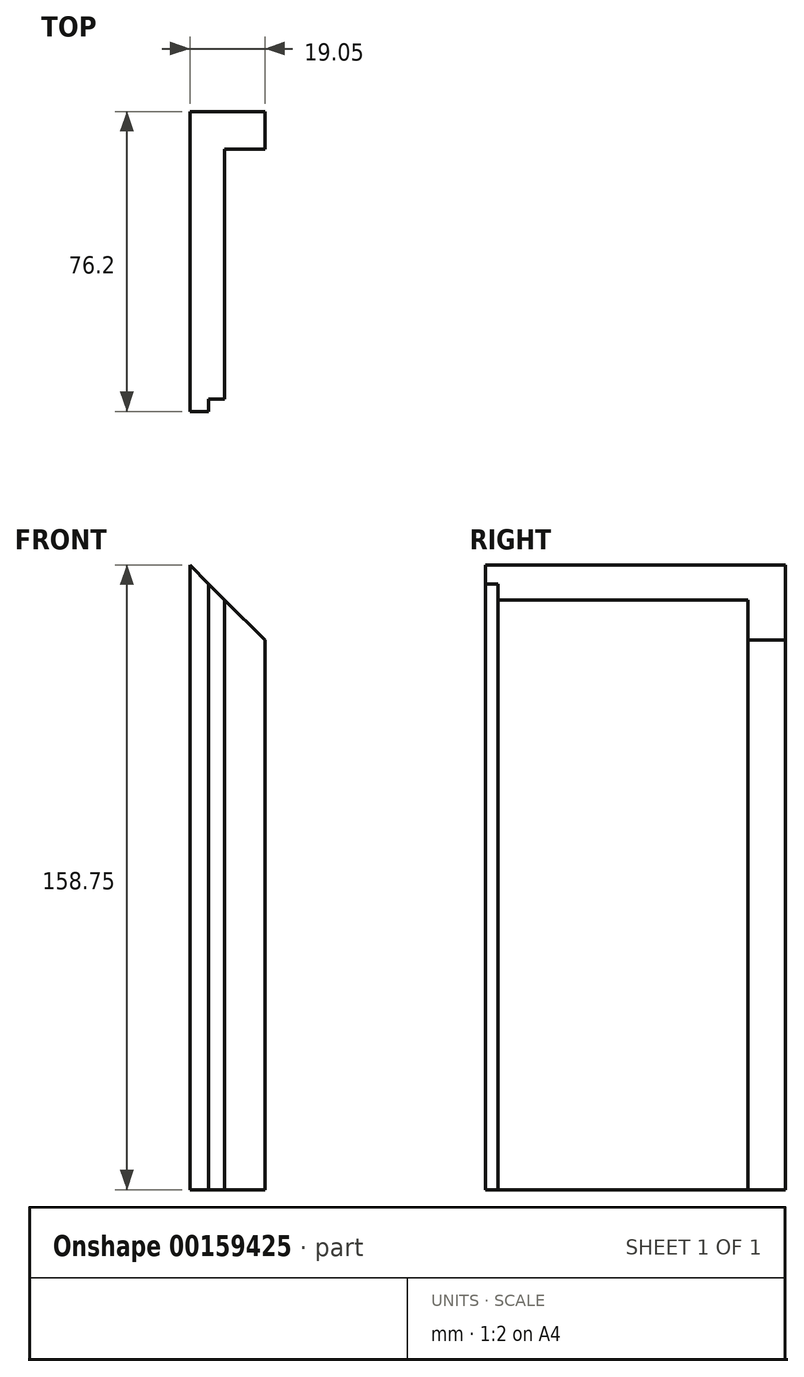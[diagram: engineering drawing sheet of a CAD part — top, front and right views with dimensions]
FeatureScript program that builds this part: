
annotation { "Feature Type Name" : "Feature", "Feature Type Description" : "" }
export const myFeature = defineFeature(function(context is Context, id is Id, definition is map)
    precondition{}
    {
        {
            var Q0;
            Q0=qCreatedBy(makeId("Front.planeOp"),FACE);
            var sketch = newSketch(context, id + "F0", { "sketchPlane" : qUnion([Q0])});
            skLineSegment(sketch, "E0", {"start": v(0, 180.55) * mm, "end": v(0, -185.02) * mm, "construction": true});
            skLineSegment(sketch, "E1", {"start": v(-187.82, 0) * mm, "end": v(184.46, 0) * mm, "construction": true});
            skLineSegment(sketch, "E2", {"start": v(0, 158.75) * mm, "end": v(-158.75, 158.75) * mm});
            skLineSegment(sketch, "E3", {"start": v(-158.75, 158.75) * mm, "end": v(-158.75, 0) * mm});
            skLineSegment(sketch, "E4", {"start": v(0, 139.7) * mm, "end": v(-139.7, 139.7) * mm});
            skLineSegment(sketch, "E5", {"start": v(-139.7, 139.7) * mm, "end": v(-139.7, 0) * mm});
            skLineSegment(sketch, "E6", {"start": v(-158.75, 0) * mm, "end": v(-139.7, 0) * mm});
            skLineSegment(sketch, "E7", {"start": v(0, 158.75) * mm, "end": v(0, 139.7) * mm});
            skSolve(sketch);
        }
        {
            var Q0;
            Q0=qSketchRegion(id+"F0",true);
            var Q1;
            Q1=qSketchRegion(id+"F2",true);
            extrude(context, id + "F1", {"entities" : qUnion([Q0, Q1]), "depth" : 76.2 * mm});
        }
        {
            var Q0;
            Q0=makeQuery(id+"F1.opExtrude","CAP_FACE",FACE,{"disambiguationData":[OSD([sQuery(id+"F0.wireOp",EDGE,"E2"),sQuery(id+"F0.wireOp",EDGE,"E3"),sQuery(id+"F0.wireOp",EDGE,"E4"),sQuery(id+"F0.wireOp",EDGE,"E5"),sQuery(id+"F0.wireOp",EDGE,"E6"),sQuery(id+"F0.wireOp",EDGE,"E7")])],"isStart":false});
            var sketch = newSketch(context, id + "F2", { "sketchPlane" : qUnion([Q0])});
            skLineSegment(sketch, "E8", {"start": v(0, -83.24) * mm, "end": v(0, 158.75) * mm, "construction": true});
            skLineSegment(sketch, "E9", {"start": v(-158.75, 0) * mm, "end": v(101.88, 0) * mm, "construction": true});
            skLineSegment(sketch, "E10.bottom", {"start": v(0, 0) * mm, "end": v(-153.92, 0) * mm});
            skLineSegment(sketch, "E10.top", {"start": v(0, 153.92) * mm, "end": v(-153.92, 153.92) * mm});
            skLineSegment(sketch, "E10.left", {"start": v(0, 0) * mm, "end": v(0, 153.92) * mm});
            skLineSegment(sketch, "E10.right", {"start": v(-153.92, 0) * mm, "end": v(-153.92, 153.92) * mm});
            skSolve(sketch);
        }
        {
            var Q0;
            Q0=qSketchRegion(id+"F2",true);
            extrude(context, id + "F3", {"entities" : qUnion([Q0]), "operationType" : NewBodyOperationType.REMOVE, "oppositeDirection" : true, "depth" : 3.17 * mm});
        }
        {
            var Q0;
            Q0=makeQuery(id+"F3.boolean.opBoolean","COPY",FACE,{"derivedFrom":makeQuery(id+"F3.opExtrude","CAP_FACE",FACE,{"disambiguationData":[OSD([sQuery(id+"F2.wireOp",EDGE,"E10.bottom"),sQuery(id+"F2.wireOp",EDGE,"E10.top"),sQuery(id+"F2.wireOp",EDGE,"E10.left"),sQuery(id+"F2.wireOp",EDGE,"E10.right")])],"isStart":false})});
            var sketch = newSketch(context, id + "F4", { "sketchPlane" : qUnion([Q0])});
            skLineSegment(sketch, "E11", {"start": v(0, 160.99) * mm, "end": v(0, -63.1) * mm, "construction": true});
            skLineSegment(sketch, "E12", {"start": v(-161.28, 0) * mm, "end": v(50.92, 0) * mm, "construction": true});
            skLineSegment(sketch, "E13.bottom", {"start": v(0, 0) * mm, "end": v(-149.86, 0) * mm});
            skLineSegment(sketch, "E13.top", {"start": v(0, 149.86) * mm, "end": v(-149.86, 149.86) * mm});
            skLineSegment(sketch, "E13.left", {"start": v(0, 0) * mm, "end": v(0, 149.86) * mm});
            skLineSegment(sketch, "E13.right", {"start": v(-149.86, 0) * mm, "end": v(-149.86, 149.86) * mm});
            skSolve(sketch);
        }
        {
            var Q0;
            Q0=qSketchRegion(id+"F4",true);
            extrude(context, id + "F5", {"entities" : qUnion([Q0]), "operationType" : NewBodyOperationType.REMOVE, "oppositeDirection" : true, "depth" : 63.5 * mm});
        }
        {
            var Q0;
            Q0=makeQuery(id+"F1.opExtrude","CAP_FACE",FACE,{"disambiguationData":[OSD([sQuery(id+"F0.wireOp",EDGE,"E2"),sQuery(id+"F0.wireOp",EDGE,"E3"),sQuery(id+"F0.wireOp",EDGE,"E4"),sQuery(id+"F0.wireOp",EDGE,"E5"),sQuery(id+"F0.wireOp",EDGE,"E6"),sQuery(id+"F0.wireOp",EDGE,"E7")])],"isStart":false});
            var sketch = newSketch(context, id + "F6", { "sketchPlane" : qUnion([Q0])});
            skPoint(sketch, "E14.0", {"position": v(-139.7, 139.7) * mm});
            skPoint(sketch, "E15.0", {"position": v(-158.75, 158.75) * mm});
            skLineSegment(sketch, "E16", {"start": v(-158.75, 158.75) * mm, "end": v(-139.7, 139.7) * mm});
            skPoint(sketch, "E17.0", {"position": v(0, 158.75) * mm});
            skPoint(sketch, "E18.0", {"position": v(0, 139.7) * mm});
            skLineSegment(sketch, "E19", {"start": v(-158.75, 158.75) * mm, "end": v(0, 158.75) * mm});
            skLineSegment(sketch, "E20", {"start": v(0, 139.7) * mm, "end": v(-139.7, 139.7) * mm});
            skLineSegment(sketch, "E21", {"start": v(0, 158.75) * mm, "end": v(0, 139.7) * mm});
            skSolve(sketch);
        }
        {
            var Q0;
            Q0 = qSketchRegion(id + "F6", true);
            extrude(context, id + "F7", {"entities" : qUnion([Q0]), "operationType" : NewBodyOperationType.REMOVE, "endBound" : BoundingType.THROUGH_ALL, "oppositeDirection" : true, "depth" : 25.4 * mm});
        }
    });
